# Revit family: 400 Wide - Low Stools
name_source: partatom
category: Furniture
units: mm (PartAtom-declared; Revit-internal decimal feet)

## family parameters
Always vertical = Yes
Cut with Voids When Loaded = No
OmniClass Number = 23.40.20.00
OmniClass Title = General Furniture and Specialties
Room Calculation Point = No
Shared = No
Work Plane-Based = No

## types (2) — shared parameters
Assembly Code = E2020200
Feet = Gresham - BLACK PLASTIC
Legs = Gresham - ASH
Manufacturer = Gresham Office Furniture
Model = GD2
Product Brochure = https://gof.co.uk
Product Data Specification = https://gof.co.uk
Range = SEATING
Seat Pad = Gresham - Camira Halcyon Aspen
URL = www.gof.co.uk

## per-type parameters (varying)
| type | A-Code | B-Code | Seat Base | Seat Pad (Vis) |
| GD2B2 | No | Yes | Gresham - Camira Halcyon Aspen | Yes |
| GD2A2 | Yes | No | Gresham - ASH | No |

note: column(s) folded — value = type name in every type: Product Code

## geometry (parser evidence)
native form markers: Sweep x3
no freeform markers — native parametric forms only
